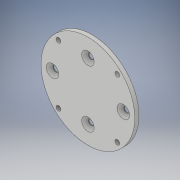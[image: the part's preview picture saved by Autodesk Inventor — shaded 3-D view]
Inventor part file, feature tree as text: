
AUTODESK INVENTOR PART (.ipt)
format: ipt  version: 2019 (Build 230136000, 136)  size: 129,536 bytes
history: native  units: mm
features: sketch x3, hole x2, extrude x1
ambient origin geometry x8: Origin, YZ Plane, XZ Plane, XY Plane, X Axis, Y Axis, Z Axis, Center Point
bodies: Solid1 (feature_tree)
feature tree (6):
  extrude  "Extrusion1"  Depth=4.0mm TaperAngle=0.0deg
  hole  "Hole1"  [1 undecoded]
  hole  "Hole2"  [1 undecoded]
  sketch  "Sketch1"  dims[d0=90.0mm d1=4.0mm d2=0.0mm]
  sketch  "Sketch2"  dims[d3=68.0mm d4=55.0mm]
  sketch  "Sketch3"  dims[d5=5.5mm d6=6.0mm d7=12.0mm d8=2.0mm d9=90.0deg d10=26.75mm d11=0.0mm d12=70.0mm d13=70.0mm d14=120.0mm d15=80.0mm d16=4.5mm d17=6.0mm d18=4.0mm d19=2.0mm d20=90.0deg d21=26.75mm d22=0.0mm]
note: 2 required parameter values undecoded (feature->parameter linkage not recoverable at this tier; creation-order binding heuristic only, values carry confidence <= 0.55)
